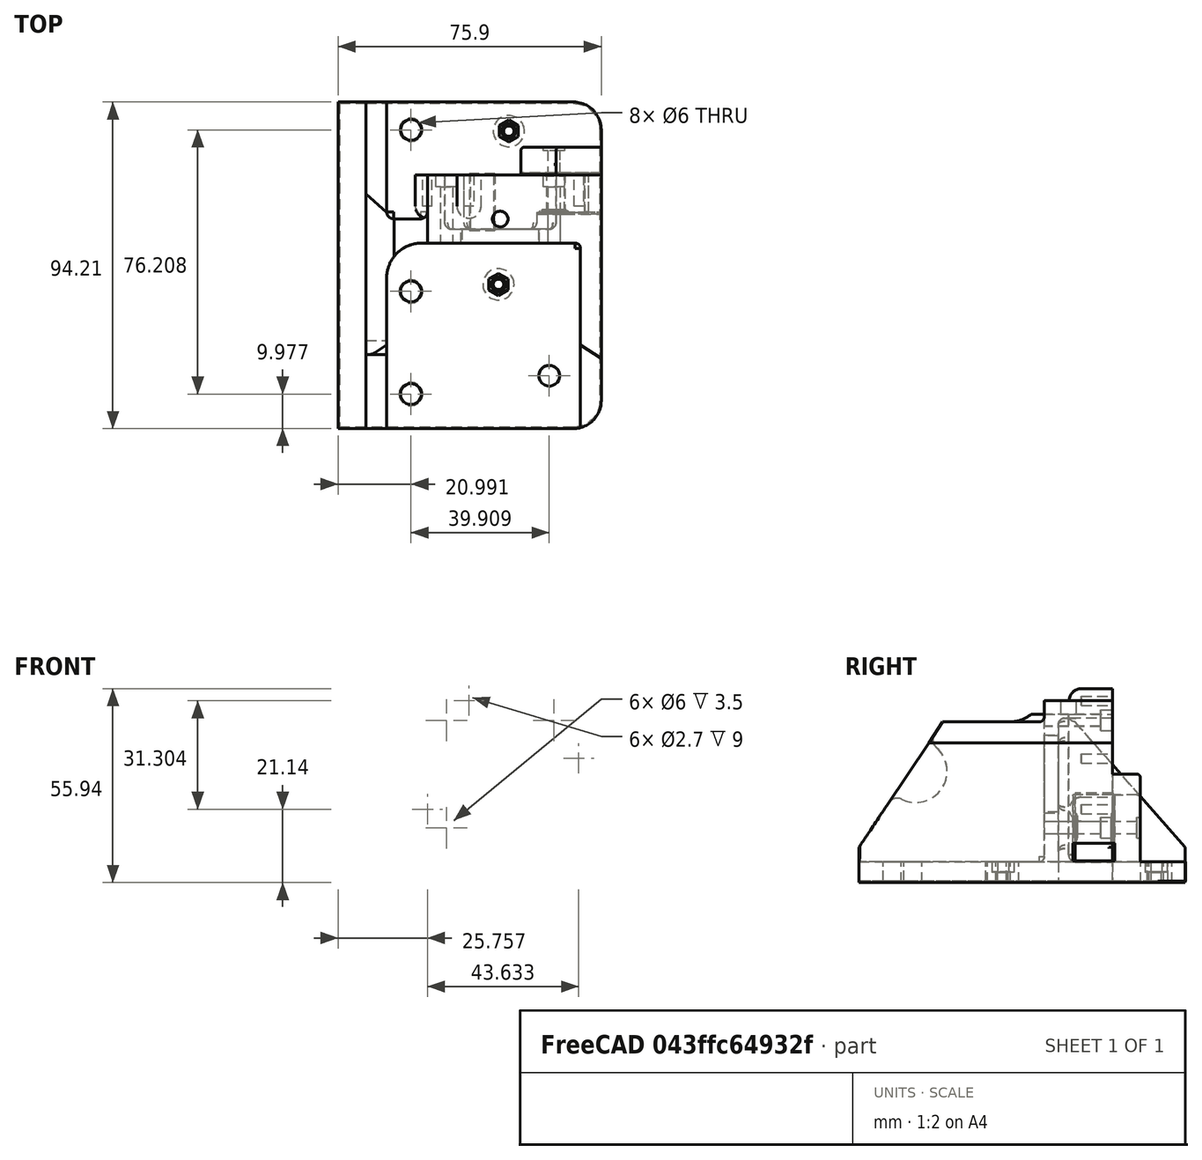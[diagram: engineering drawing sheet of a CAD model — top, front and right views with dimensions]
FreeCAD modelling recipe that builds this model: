
FCSTD DOCUMENT  (FreeCAD 0.18R16146 (Git))
Label: motor-mount-left-2
License: All rights reserved
LicenseURL: http://en.wikipedia.org/wiki/All_rights_reserved
objects: Part::Cylinder×10, Part::Cut×7, Part::Feature×4, Part::Chamfer×3, Part::MultiFuse×2
note: 26 computed .brp shape members not serialized (recipe doc carries the construction recipe); baked Part::Feature solids carry a one-line shape summary decoded from their .brp

FEATURE [Part::Feature] Part__Feature175  label="MotorBracket_LEFT_Body (1)"
  Placement = pos=(4.25,-428.83,-465.21) rot=(0,0,1;0rad)
  shape: bbox 75.9 x 94.2 x 55.94 mm, 170 faces (baked)
FEATURE [Part::Feature] Part__Feature102  label="MotorBracket_LEFT_Body (1)001"
  Placement = pos=(4.24887,-428.826,-465.206) rot=(0,-0.688997,-0.724764;0rad)
  shape: bbox 75.9 x 94.2 x 55.94 mm, 174 faces (baked)
FEATURE [Part::Cylinder] Cylinder
  Angle = 360
  AttacherType = Attacher::AttachEngine3D
  Height = 11
  Placement = pos=(62.25,62.325,15.8) rot=(-1,0,0;1.5708rad)
  Radius = 10
FEATURE [Part::Cylinder] Cylinder001
  Angle = 360
  AttacherType = Attacher::AttachEngine3D
  Height = 0.75
  Placement = pos=(62.25,62.325,15.8) rot=(-1,0,0;1.5708rad)
  Radius = 3.5
FEATURE [Part::Cut] Cut
  Base = -> Part__Feature102
  Tool = -> Cylinder
FEATURE [Part::Cylinder] Cylinder002
  Angle = 360
  AttacherType = Attacher::AttachEngine3D
  Height = 0.75
  Placement = pos=(62.25,62.325,15.8) rot=(-1,0,0;1.5708rad)
  Radius = 1.6
FEATURE [Part::Chamfer] Chamfer
  Base = -> Cut
  Edges = 17 edges r=0.4: [Edge55,Edge67,Edge69,Edge132,Edge135,Edge137,Edge139,Edge172,Edge195,Edge198,Edge199,Edge200,Edge201,Edge202,Edge203,Edge204,Edge205]
FEATURE [Part::Cylinder] Cylinder003
  Angle = 360
  AttacherType = Attacher::AttachEngine3D
  Height = 10
  Placement = pos=(46.74,51,31.29) rot=(-1,0,0;1.5708rad)
  Radius = 11.25
FEATURE [Part::Cut] Cut001003
  Base = -> Cylinder001
  Tool = -> Cylinder002
FEATURE [Part::Feature] Cut001003001  label="Cut001004"
  Placement = pos=(0,-0.35,0) rot=(0,0,1;0rad)
  shape: bbox 7 x 0.75 x 7 mm, 4 faces (baked)
FEATURE [Part::Feature] Cut001003002  label="Cut001005"
  Placement = pos=(0,10.6,0) rot=(0,0,1;0rad)
  shape: bbox 7 x 0.75 x 7 mm, 4 faces (baked)
FEATURE [Part::Chamfer] Chamfer001
  Base = -> Cut001003002
  Edges = 1 edges r=0.5: [Edge3]
FEATURE [Part::Chamfer] Chamfer002
  Base = -> Cut001003001
  Edges = 1 edges r=0.5: [Edge1]
FEATURE [Part::MultiFuse] Fusion
  Shapes = -> [Chamfer002,Chamfer001]
FEATURE [Part::Cut] Cut001003003
  Base = -> Chamfer
  Tool = -> Cylinder003
FEATURE [Part::MultiFuse] Fusion001
  Shapes = -> [Cut001003003,Fusion]
FEATURE [Part::Cylinder] Cylinder004
  Angle = 360
  AttacherType = Attacher::AttachEngine3D
  Height = 6
  Placement = pos=(46.25,41.59,0) rot=(0,0,1;0rad)
  Radius = 2.1
FEATURE [Part::Cylinder] Cylinder005
  Angle = 360
  AttacherType = Attacher::AttachEngine3D
  Height = 6
  Placement = pos=(49.25,85.81,0) rot=(0,0,1;0rad)
  Radius = 2.1
FEATURE [Part::Cylinder] Cylinder006
  Angle = 360
  AttacherType = Attacher::AttachEngine3D
  Height = 6
  Placement = pos=(49.25,85.81,0) rot=(0,0,1;0rad)
  Radius = 4.5
FEATURE [Part::Cylinder] Cylinder007
  Angle = 360
  AttacherType = Attacher::AttachEngine3D
  Height = 6
  Placement = pos=(46.25,41.59,0) rot=(0,0,1;0rad)
  Radius = 4.5
FEATURE [Part::Cylinder] Cylinder008
  Angle = 360
  AttacherType = Attacher::AttachEngine3D
  Height = 6
  Placement = pos=(49.25,85.81,0) rot=(0,0,1;0rad)
  Radius = 2.1
FEATURE [Part::Cylinder] Cylinder009
  Angle = 360
  AttacherType = Attacher::AttachEngine3D
  Height = 6
  Placement = pos=(46.25,41.59,0) rot=(0,0,1;0rad)
  Radius = 2.1
FEATURE [Part::Cut] Cut001003004
  Base = -> Fusion001
  Tool = -> Cylinder008
FEATURE [Part::Cut] Cut001003005
  Base = -> Cut001003004
  Tool = -> Cylinder009
FEATURE [Part::Cut] Cut001003006
  Base = -> Cylinder006
  Tool = -> Cylinder005
FEATURE [Part::Cut] Cut001003007
  Base = -> Cylinder007
  Tool = -> Cylinder004
